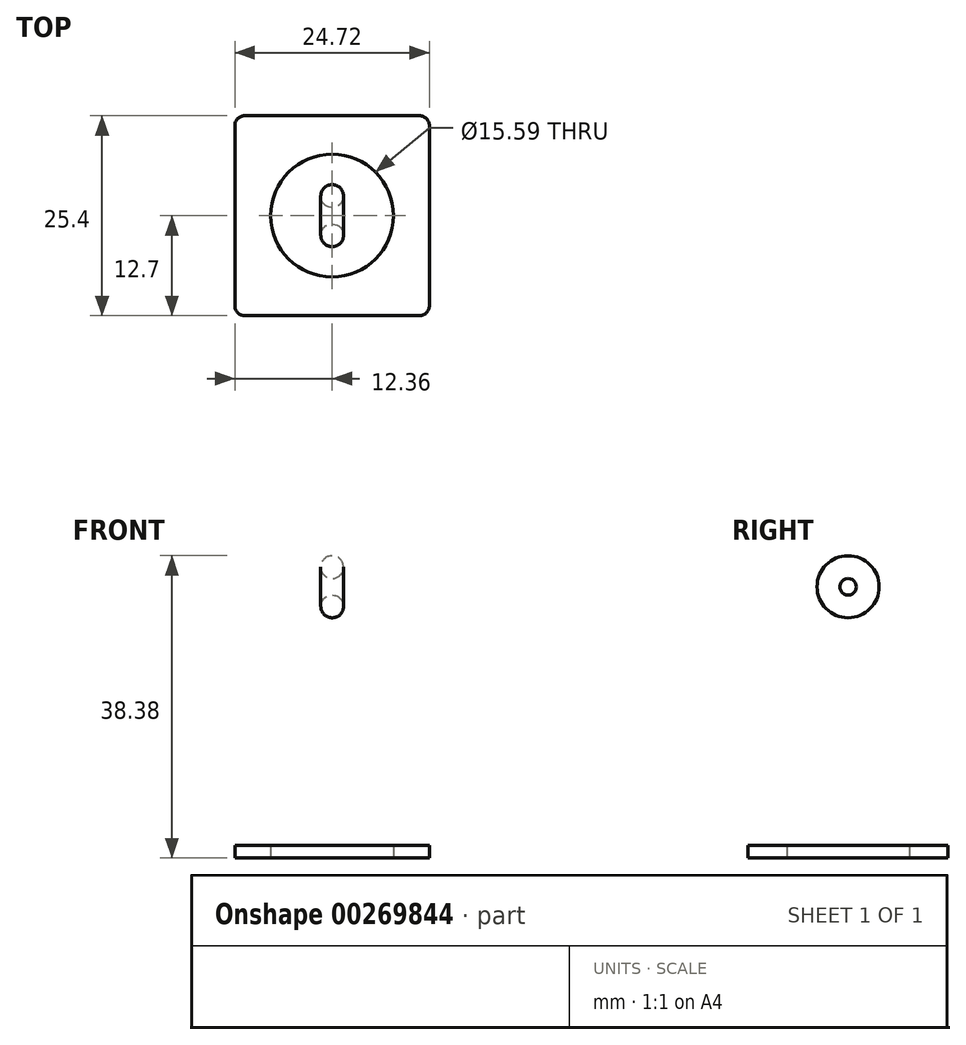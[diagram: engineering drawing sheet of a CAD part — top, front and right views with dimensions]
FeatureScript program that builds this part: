
annotation { "Feature Type Name" : "Feature", "Feature Type Description" : "" }
export const myFeature = defineFeature(function(context is Context, id is Id, definition is map)
    precondition{}
    {
        {
            var Q0;
            Q0=qCreatedBy(makeId("Top.planeOp"),FACE);
            var sketch = newSketch(context, id + "F0", { "sketchPlane" : qUnion([Q0])});
            skLineSegment(sketch, "E0.bottom", {"start": v(11.1, -12.7) * mm, "end": v(-11.1, -12.7) * mm});
            skLineSegment(sketch, "E0.top", {"start": v(11.1, 12.7) * mm, "end": v(-11.1, 12.7) * mm});
            skLineSegment(sketch, "E0.left", {"start": v(12.36, -11.43) * mm, "end": v(12.36, 11.43) * mm});
            skLineSegment(sketch, "E0.right", {"start": v(-12.36, -11.43) * mm, "end": v(-12.36, 11.43) * mm});
            skPoint(sketch, "E0.middle", {"position": v(0, 0) * mm});
            skPoint(sketch, "E1.visualSharp", {"position": v(-12.36, 12.7) * mm});
            skArc(sketch, "E1.filletArc", {"start": v(-11.1, 12.7) * mm, "mid": v(-12, 12.33) * mm, "end": v(-12.36, 11.43) * mm});
            skPoint(sketch, "E2.visualSharp", {"position": v(12.36, 12.7) * mm});
            skArc(sketch, "E2.filletArc", {"start": v(12.36, 11.43) * mm, "mid": v(12, 12.33) * mm, "end": v(11.1, 12.7) * mm});
            skPoint(sketch, "E3.visualSharp", {"position": v(12.36, -12.7) * mm});
            skArc(sketch, "E3.filletArc", {"start": v(11.1, -12.7) * mm, "mid": v(12, -12.33) * mm, "end": v(12.36, -11.43) * mm});
            skPoint(sketch, "E4.visualSharp", {"position": v(-12.36, -12.7) * mm});
            skArc(sketch, "E4.filletArc", {"start": v(-12.36, -11.43) * mm, "mid": v(-12, -12.33) * mm, "end": v(-11.1, -12.7) * mm});
            skSolve(sketch);
        }
        {
            var Q0;
            Q0=makeQuery(id+"F0.imprint","IMPRINT",FACE,{"disambiguationData":[TD([[makeQuery(id+"F0.imprint","IMPRINT",EDGE,{"derivedFrom":sQuery(id+"F0.wireOp",EDGE,"E0.bottom")}),-1.0]])]});
            extrude(context, id + "F1", {"entities" : qUnion([Q0]), "depth" : 1.59 * mm});
        }
        {
            var Q0;
            Q0=qCreatedBy(makeId("Front.planeOp"),FACE);
            var sketch = newSketch(context, id + "F2", { "sketchPlane" : qUnion([Q0])});
            skLineSegment(sketch, "E5", {"start": v(-8.9, 1.63) * mm, "end": v(-1.59, 31.22) * mm});
            skLineSegment(sketch, "E6", {"start": v(-1.59, 31.22) * mm, "end": v(0, 31.22) * mm});
            skPoint(sketch, "E7.end.orphan", {"position": v(0, 1.63) * mm});
            skLineSegment(sketch, "E8", {"start": v(-8.9, 1.63) * mm, "end": v(-7.79, 1.63) * mm});
            skLineSegment(sketch, "E9", {"start": v(-7.79, 1.63) * mm, "end": v(-0.88, 30.05) * mm});
            skLineSegment(sketch, "E10", {"start": v(-0.88, 30.05) * mm, "end": v(0, 30.05) * mm});
            skLineSegment(sketch, "E11", {"start": v(0, 30.05) * mm, "end": v(0, 31.22) * mm});
            skSolve(sketch);
        }
        {
            var Q0;
            Q0=sQuery(id+"F2.wireOp",EDGE,"E5");
            var Q1;
            Q1=sQuery(id+"F2.wireOp",EDGE,"E6");
            var Q2;
            Q2=sQuery(id+"F2.wireOp",EDGE,"dKXRRnsz-az8R-Xcw6-1ReQ-hhXjo8uIubkW");
            var Q3;
            Q3=sQuery(id+"F2.wireOp",EDGE,"E11");
            revolve(context, id + "F3", {"bodyType" : ToolBodyType.SURFACE, "surfaceEntities" : qUnion([Q0, Q1, Q2]), "axis" : qUnion([Q3]), "revolveType" : RevolveType.FULL});
        }
        {
            var Q0;
            Q0=qCreatedBy(makeId("Front.planeOp"),FACE);
            var sketch = newSketch(context, id + "F4", { "sketchPlane" : qUnion([Q0])});
            skCircle(sketch, "E12", {"center": v(0, 31.94) * mm, "radius": 1.45 * mm});
            skLineSegment(sketch, "E13", {"start": v(-2.7, 34.43) * mm, "end": v(3.17, 34.43) * mm});
            skSolve(sketch);
        }
        {
            var Q0;
            Q0=makeQuery(id+"F4.imprint","IMPRINT",FACE,{"disambiguationData":[TD([[makeQuery(id+"F4.imprint","IMPRINT",EDGE,{"derivedFrom":sQuery(id+"F4.wireOp",EDGE,"E12")}),1.0]])]});
            var Q1;
            Q1=sQuery(id+"F4.wireOp",EDGE,"E13");
            revolve(context, id + "F5", {"entities" : qUnion([Q0]), "axis" : qUnion([Q1]), "revolveType" : RevolveType.FULL});
        }
        {
            var Q0;
            Q0=qCreatedBy(makeId("Top.planeOp"),FACE);
            var sketch = newSketch(context, id + "F6", { "sketchPlane" : qUnion([Q0])});
            skCircle(sketch, "E14", {"center": v(0, 0) * mm, "radius": 7.8 * mm});
            skSolve(sketch);
        }
        {
            var Q0;
            Q0=qSketchRegion(id+"F6",true);
            extrude(context, id + "F7", {"entities" : qUnion([Q0]), "operationType" : NewBodyOperationType.REMOVE, "depth" : 1.65 * mm});
        }
    });
